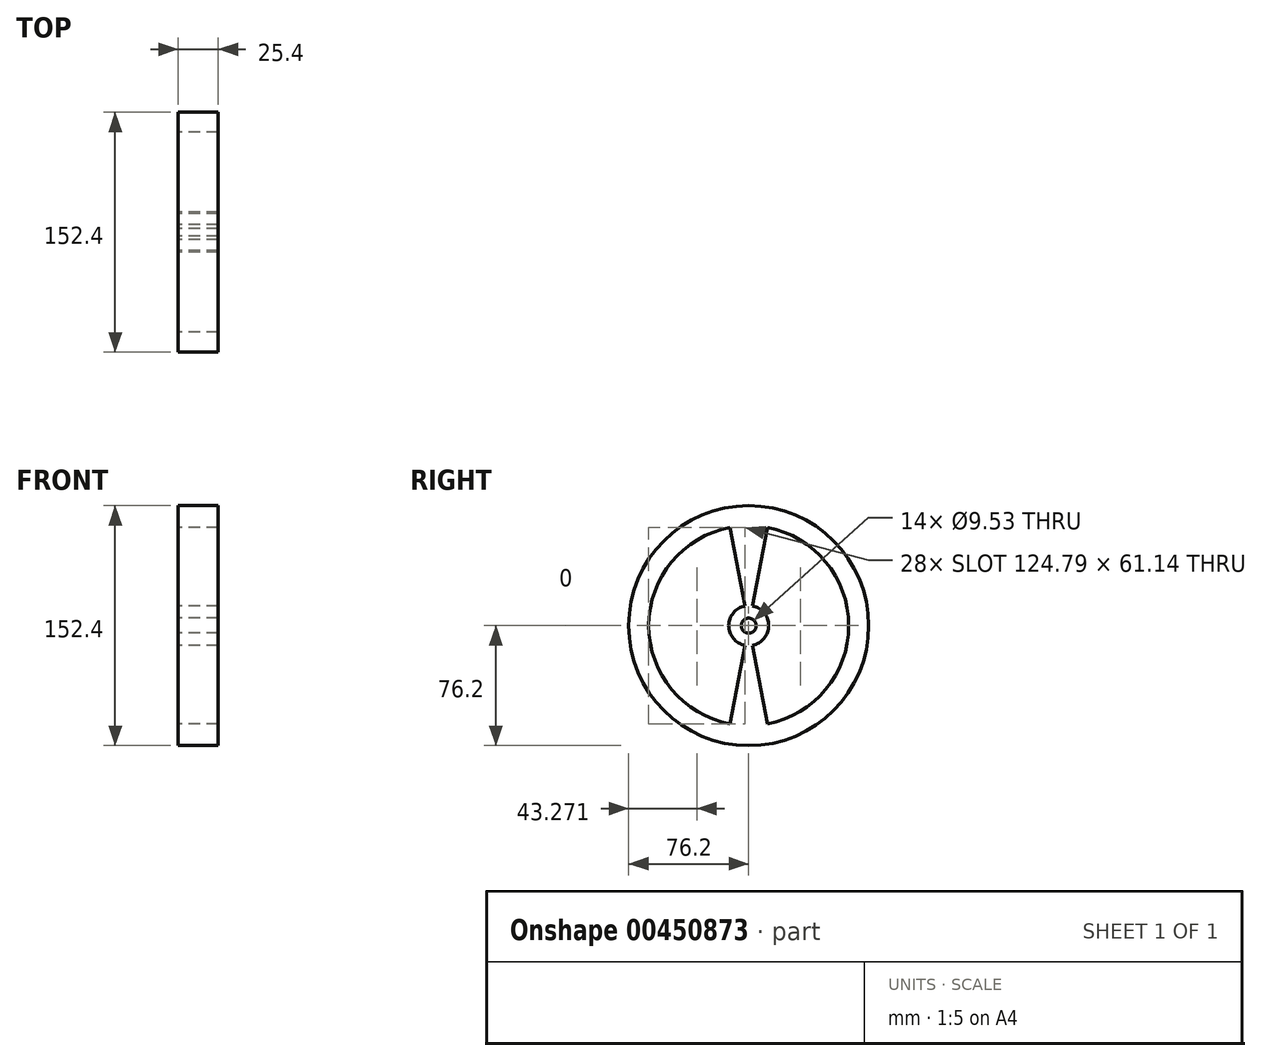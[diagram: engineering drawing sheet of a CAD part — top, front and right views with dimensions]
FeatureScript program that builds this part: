
annotation { "Feature Type Name" : "Feature", "Feature Type Description" : "" }
export const myFeature = defineFeature(function(context is Context, id is Id, definition is map)
    precondition{}
    {
        {
            var Q0;
            Q0=qCreatedBy(makeId("Right.planeOp"),FACE);
            var sketch = newSketch(context, id + "F0", { "sketchPlane" : qUnion([Q0])});
            skCircle(sketch, "E0", {"center": v(0, 0) * mm, "radius": 76.2 * mm});
            skCircle(sketch, "E1", {"center": v(0, 0) * mm, "radius": 63.5 * mm});
            skLineSegment(sketch, "E2.MirrorCS", {"start": v(-2.36, -12.48) * mm, "end": v(-11.8, -62.4) * mm});
            skLineSegment(sketch, "E3.MirrorCS", {"start": v(2.36, -12.48) * mm, "end": v(11.8, -62.4) * mm});
            skCircle(sketch, "E4", {"center": v(0, 0) * mm, "radius": 12.7 * mm});
            skCircle(sketch, "E5", {"center": v(0, 0) * mm, "radius": 4.76 * mm});
            skLineSegment(sketch, "E6.trimOffspring", {"start": v(-2.36, 12.48) * mm, "end": v(-11.8, 62.4) * mm});
            skLineSegment(sketch, "E7.trimOffspring", {"start": v(2.36, 12.48) * mm, "end": v(11.8, 62.4) * mm});
            skSolve(sketch);
        }
        {
            var Q0;
            Q0=qSketchRegion(id+"F0",true);
            var Q1;
            {var subQ0=sQuery(id+"F0.wireOp",EDGE,"E6.trimOffspring");Q1=makeQuery(id+"F0.imprint","IMPRINT",FACE,{"disambiguationData":[TD([[makeQuery(id+"F0.imprint","IMPRINT",EDGE,{"derivedFrom":subQ0}),-1.0]])]});}
            var Q2;
            Q2=makeQuery(id+"F0.imprint","IMPRINT",FACE,{"disambiguationData":[TD([[makeQuery(id+"F0.imprint","IMPRINT",EDGE,{"derivedFrom":sQuery(id+"F0.wireOp",EDGE,"E5")}),-1.0]])]});
            var Q3;
            {var subQ0=sQuery(id+"F0.wireOp",EDGE,"E2.MirrorCS");Q3=makeQuery(id+"F0.imprint","IMPRINT",FACE,{"disambiguationData":[TD([[makeQuery(id+"F0.imprint","IMPRINT",EDGE,{"derivedFrom":subQ0}),1.0]])]});}
            extrude(context, id + "F1", {"entities" : qUnion([Q0, Q1, Q2, Q3]), "depth" : 25.4 * mm});
        }
    });
